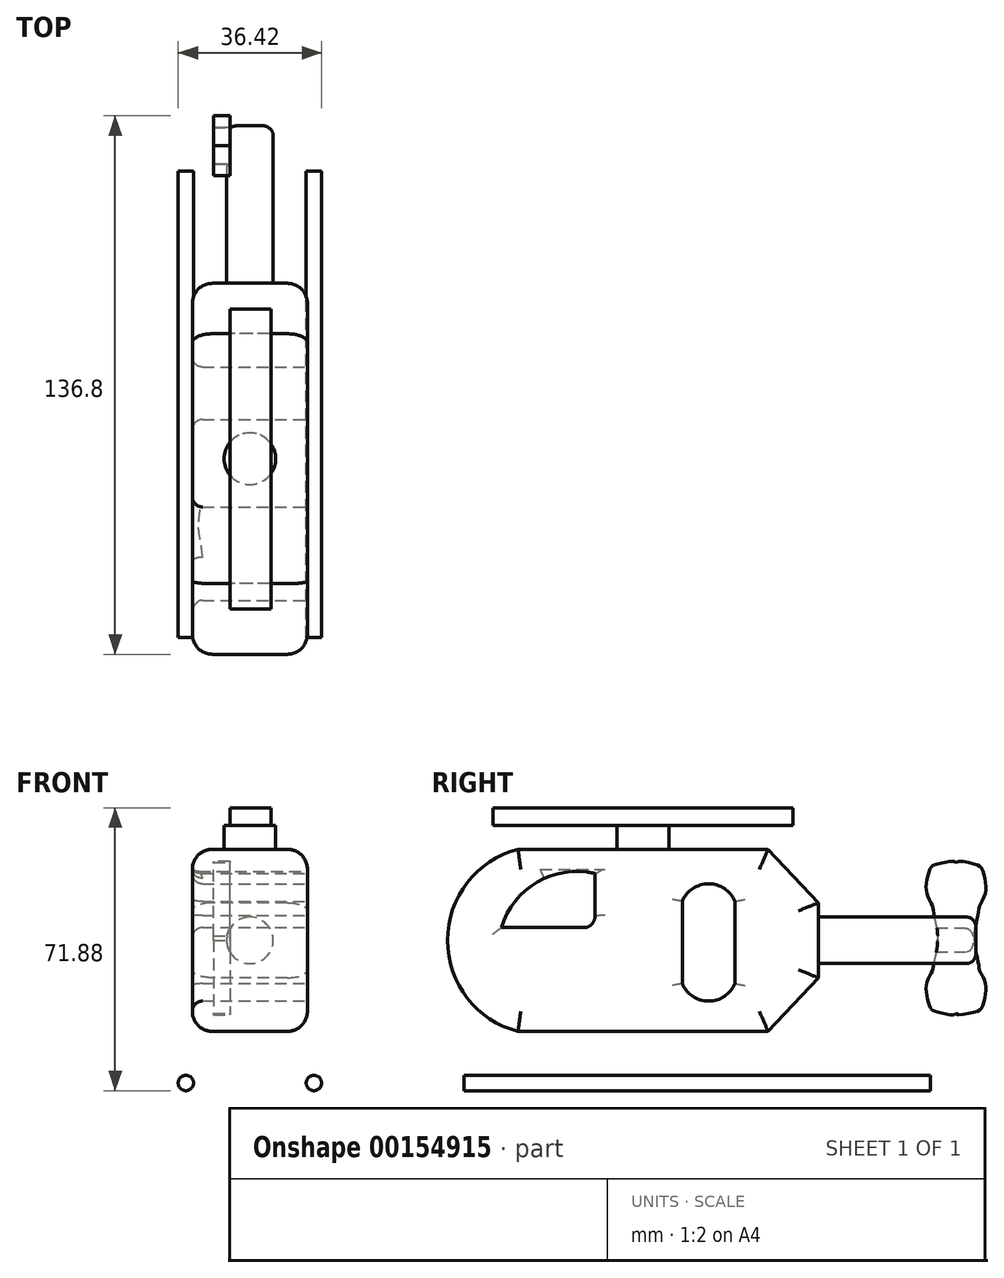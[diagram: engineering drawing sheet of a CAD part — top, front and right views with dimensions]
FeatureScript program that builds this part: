
annotation { "Feature Type Name" : "Feature", "Feature Type Description" : "" }
export const myFeature = defineFeature(function(context is Context, id is Id, definition is map)
    precondition{}
    {
        {
            var Q0;
            Q0=qCreatedBy(makeId("Right.planeOp"),FACE);
            var sketch = newSketch(context, id + "F0", { "sketchPlane" : qUnion([Q0])});
            skLineSegment(sketch, "E0", {"start": v(-45.55, 0) * mm, "end": v(17.95, 0) * mm});
            skLineSegment(sketch, "E1", {"start": v(-45.55, 46.28) * mm, "end": v(17.95, 46.28) * mm});
            skArc(sketch, "E2", {"start": v(-45.55, 46.28) * mm, "mid": v(-63.48, 23.14) * mm, "end": v(-45.55, 0) * mm});
            skLineSegment(sketch, "E3", {"start": v(17.95, 0) * mm, "end": v(30.77, 13.61) * mm});
            skLineSegment(sketch, "E4", {"start": v(-82.92, 23.14) * mm, "end": v(97.5, 23.14) * mm, "construction": true});
            skPoint(sketch, "E4.endSnap0", {"position": v(-63.48, 23.14) * mm});
            skLineSegment(sketch, "E5.MirrorCS", {"start": v(17.95, 46.28) * mm, "end": v(30.77, 32.66) * mm});
            skLineSegment(sketch, "E6", {"start": v(30.77, 32.66) * mm, "end": v(30.77, 13.61) * mm});
            skSolve(sketch);
        }
        {
            var Q0;
            Q0=makeQuery(id+"F0.imprint","IMPRINT",FACE,{"disambiguationData":[TD([[makeQuery(id+"F0.imprint","IMPRINT",EDGE,{"derivedFrom":sQuery(id+"F0.wireOp",EDGE,"E0")}),1.0]])]});
            extrude(context, id + "F1", {"entities" : qUnion([Q0]), "endBound" : BoundingType.SYMMETRIC, "depth" : 29.2 * mm});
        }
        {
            var Q0;
            Q0=makeQuery(id+"F1.opExtrude","CAP_FACE",FACE,{"disambiguationData":[OSD([sQuery(id+"F0.wireOp",EDGE,"E0"),sQuery(id+"F0.wireOp",EDGE,"E1"),sQuery(id+"F0.wireOp",EDGE,"E2"),sQuery(id+"F0.wireOp",EDGE,"E3"),sQuery(id+"F0.wireOp",EDGE,"E5.MirrorCS"),sQuery(id+"F0.wireOp",EDGE,"E6")])],"isStart":false});
            var sketch = newSketch(context, id + "F2", { "sketchPlane" : qUnion([Q0])});
            skLineSegment(sketch, "E7", {"start": v(-49.76, 26.38) * mm, "end": v(-28.82, 26.38) * mm});
            skLineSegment(sketch, "E8", {"start": v(-26.07, 29.47) * mm, "end": v(-26.07, 40.12) * mm});
            skArc(sketch, "E9", {"start": v(-26.07, 40.12) * mm, "mid": v(-40.65, 37.96) * mm, "end": v(-49.76, 26.38) * mm});
            skArc(sketch, "E10", {"start": v(-28.82, 26.38) * mm, "mid": v(-26.75, 27.3) * mm, "end": v(-26.07, 29.47) * mm});
            skLineSegment(sketch, "E11", {"start": v(-3.85, 33.03) * mm, "end": v(-3.85, 12.15) * mm});
            skLineSegment(sketch, "E12", {"start": v(9.5, 33.03) * mm, "end": v(9.5, 12.15) * mm});
            skArc(sketch, "E13", {"start": v(9.5, 33.03) * mm, "mid": v(2.83, 37.49) * mm, "end": v(-3.85, 33.03) * mm});
            skLineSegment(sketch, "E14", {"start": v(-8.12, 22.6) * mm, "end": v(-3.85, 22.6) * mm, "construction": true});
            skPoint(sketch, "E14.startSnap0", {"position": v(-3.85, 22.6) * mm});
            skArc(sketch, "E15.MirrorCS", {"start": v(9.5, 12.15) * mm, "mid": v(2.83, 7.7) * mm, "end": v(-3.85, 12.15) * mm});
            skLineSegment(sketch, "E16.trimOffspring", {"start": v(9.5, 22.6) * mm, "end": v(12.31, 22.6) * mm, "construction": true});
            skSolve(sketch);
        }
        {
            var Q0;
            Q0 = qSketchRegion(id + "F2", true);
            extrude(context, id + "F3", {"entities" : qUnion([Q0]), "operationType" : NewBodyOperationType.ADD, "depth" : 25.4 * mm});
        }
        {
            var Q0;
            Q0=makeQuery(id+"F3.opExtrude","CAP_FACE",FACE,{"disambiguationData":[OSD([sQuery(id+"F2.wireOp",EDGE,"E7"),sQuery(id+"F2.wireOp",EDGE,"E8"),sQuery(id+"F2.wireOp",EDGE,"E9"),sQuery(id+"F2.wireOp",EDGE,"E10")])],"isStart":false});
            extrude(context, id + "F4", {"entities" : qUnion([Q0]), "operationType" : NewBodyOperationType.REMOVE, "oppositeDirection" : true, "depth" : 77.47 * mm});
        }
        {
            var Q0;
            Q0=makeQuery(id+"F3.opExtrude","CAP_FACE",FACE,{"disambiguationData":[OSD([sQuery(id+"F2.wireOp",EDGE,"E11"),sQuery(id+"F2.wireOp",EDGE,"E12"),sQuery(id+"F2.wireOp",EDGE,"E13"),sQuery(id+"F2.wireOp",EDGE,"E15.MirrorCS")])],"isStart":false});
            extrude(context, id + "F5", {"entities" : qUnion([Q0]), "operationType" : NewBodyOperationType.REMOVE, "oppositeDirection" : true, "depth" : 73.02 * mm});
        }
        {
            var Q0;
            Q0=makeQuery(id+"F1.opExtrude","SWEPT_FACE",FACE,{"disambiguationData":[OSD([sQuery(id+"F0.wireOp",EDGE,"E6")])]});
            var sketch = newSketch(context, id + "F6", { "sketchPlane" : qUnion([Q0])});
            skCircle(sketch, "E17", {"center": v(0, 23.14) * mm, "radius": 5.92 * mm});
            skPoint(sketch, "E17.centerSnap0", {"position": v(-14.6, 23.14) * mm});
            skPoint(sketch, "E17.centerSnap1", {"position": v(0, 32.66) * mm});
            skSolve(sketch);
        }
        {
            var Q0;
            Q0=makeQuery(id+"F6.imprint","IMPRINT",FACE,{"disambiguationData":[TD([[makeQuery(id+"F6.imprint","IMPRINT",EDGE,{"derivedFrom":sQuery(id+"F6.wireOp",EDGE,"E17")}),1.0]])]});
            extrude(context, id + "F7", {"entities" : qUnion([Q0]), "operationType" : NewBodyOperationType.ADD, "depth" : 40 * mm});
        }
        {
            var Q0;
            Q0=qCreatedBy(makeId("Right.planeOp"),FACE);
            cPlane(context, id + "F8", {"entities" : qUnion([Q0]), "cplaneType" : CPlaneType.OFFSET, "offset" : 5.08 * mm, "oppositeDirection" : true, "width" : 152.4 * mm, "height" : 152.4 * mm});
        }
        {
            var Q0;
            Q0=qCreatedBy(id+"F8.planeOp",FACE);
            var sketch = newSketch(context, id + "F9", { "sketchPlane" : qUnion([Q0])});
            skCircle(sketch, "E18", {"center": v(65.71, 23.72) * mm, "radius": 4.7 * mm});
            skFitSpline(sketch, "E19", {"points": [v(70.41, 23.72) * mm, v(71.36, 29.92) * mm, v(71.72, 31.94) * mm, v(73.1, 34.83) * mm, v(73.17, 38.08) * mm, v(72.23, 41.47) * mm, v(70.5, 42.48) * mm, v(65.71, 42.91) * mm, v(65.71, 42.35) * mm], "startDerivative": vector(-3.63, 35.2) * mm, "endDerivative": vector(2.3, 5.08) * mm});
            skLineSegment(sketch, "E20", {"start": v(65.71, 42.91) * mm, "end": v(65.71, 6.47) * mm, "construction": true});
            skLineSegment(sketch, "E21", {"start": v(61.01, 23.72) * mm, "end": v(70.41, 23.72) * mm, "construction": true});
            skFitSpline(sketch, "E22.MirrorCS", {"points": [v(61.01, 23.72) * mm, v(60.06, 29.92) * mm, v(59.7, 31.94) * mm, v(58.33, 34.83) * mm, v(58.26, 38.08) * mm, v(59.2, 41.47) * mm, v(60.93, 42.48) * mm, v(65.71, 42.91) * mm, v(65.71, 42.35) * mm], "startDerivative": vector(3.63, 35.2) * mm, "endDerivative": vector(-2.3, 5.08) * mm});
            skFitSpline(sketch, "E23.MirrorCS", {"points": [v(70.41, 23.72) * mm, v(71.36, 17.51) * mm, v(71.72, 15.5) * mm, v(73.1, 12.6) * mm, v(73.17, 9.36) * mm, v(72.23, 5.96) * mm, v(70.5, 4.95) * mm, v(65.71, 4.52) * mm, v(65.71, 5.08) * mm], "startDerivative": vector(-3.63, -35.2) * mm, "endDerivative": vector(2.3, -5.08) * mm});
            skFitSpline(sketch, "E24.MirrorCS", {"points": [v(61.01, 23.72) * mm, v(60.06, 17.51) * mm, v(59.7, 15.5) * mm, v(58.33, 12.6) * mm, v(58.26, 9.36) * mm, v(59.2, 5.96) * mm, v(60.93, 4.95) * mm, v(65.71, 4.52) * mm, v(65.71, 5.08) * mm], "startDerivative": vector(3.63, -35.2) * mm, "endDerivative": vector(-2.3, -5.08) * mm});
            skSolve(sketch);
        }
        {
            var Q0;
            Q0=makeQuery(id+"F1.opExtrude","SWEPT_FACE",FACE,{"disambiguationData":[OSD([sQuery(id+"F0.wireOp",EDGE,"E1")])]});
            var sketch = newSketch(context, id + "F10", { "sketchPlane" : qUnion([Q0])});
            skLineSegment(sketch, "E25", {"start": v(0, 17.95) * mm, "end": v(0, -45.55) * mm, "construction": true});
            skLineSegment(sketch, "E26", {"start": v(14.6, -13.8) * mm, "end": v(-14.6, -13.8) * mm, "construction": true});
            skCircle(sketch, "E27", {"center": v(0, -13.8) * mm, "radius": 6.57 * mm});
            skSolve(sketch);
        }
        {
            var Q0;
            Q0 = qSketchRegion(id + "F10", true);
            extrude(context, id + "F11", {"entities" : qUnion([Q0]), "operationType" : NewBodyOperationType.ADD, "depth" : 6.1 * mm});
        }
        {
            var Q0;
            Q0 = qSketchRegion(id + "F9", true);
            extrude(context, id + "F12", {"entities" : qUnion([Q0]), "operationType" : NewBodyOperationType.ADD, "oppositeDirection" : true, "depth" : 4.2 * mm});
        }
        {
            var Q0;
            Q0=makeQuery(id+"F11.opExtrude","CAP_FACE",FACE,{"disambiguationData":[OSD([sQuery(id+"F10.wireOp",EDGE,"E27")])],"isStart":false});
            var sketch = newSketch(context, id + "F13", { "sketchPlane" : qUnion([Q0])});
            skLineSegment(sketch, "E28.bottom", {"start": v(-5.08, 24.28) * mm, "end": v(5.38, 24.28) * mm});
            skLineSegment(sketch, "E28.top", {"start": v(-5.08, -51.92) * mm, "end": v(5.38, -51.92) * mm});
            skLineSegment(sketch, "E28.left", {"start": v(-5.08, 24.28) * mm, "end": v(-5.08, -51.92) * mm});
            skLineSegment(sketch, "E28.right", {"start": v(5.38, 24.28) * mm, "end": v(5.38, -51.92) * mm});
            skSolve(sketch);
        }
        {
            var Q0;
            {var subQ0=sQuery(id+"F13.wireOp",EDGE,"E28.bottom");Q0=makeQuery(id+"F13.imprint","IMPRINT",FACE,{"disambiguationData":[TD([[makeQuery(id+"F13.imprint","IMPRINT",EDGE,{"derivedFrom":subQ0}),-1.0]])]});}
            var Q1;
            {var subQ0=sQuery(id+"F13.wireOp",EDGE,"E28.left");var subQ1=makeQuery(id+"F11.opExtrude","CAP_EDGE",EDGE,{"disambiguationData":[OSD([sQuery(id+"F10.wireOp",EDGE,"E27")])],"isStart":false});var subQ2=makeQuery(id+"F13.imprint","INTERSECT",VERTEX,{"disambiguationData":[OD(0.0)],"derivedFrom":[subQ1,subQ0]});Q1=makeQuery(id+"F13.imprint","IMPRINT",FACE,{"disambiguationData":[TD([[makeQuery(id+"F13.imprint","IMPRINT",EDGE,{"disambiguationData":[TD([[subQ2,-1.0]])],"derivedFrom":subQ0}),1.0]])]});}
            var Q2;
            {var subQ0=sQuery(id+"F13.wireOp",EDGE,"E28.top");Q2=makeQuery(id+"F13.imprint","IMPRINT",FACE,{"disambiguationData":[TD([[makeQuery(id+"F13.imprint","IMPRINT",EDGE,{"derivedFrom":subQ0}),1.0]])]});}
            extrude(context, id + "F14", {"entities" : qUnion([Q0, Q1, Q2]), "operationType" : NewBodyOperationType.ADD, "depth" : 4.44 * mm});
        }
        {
            var Q0;
            Q0=qCreatedBy(makeId("Front.planeOp"),FACE);
            var sketch = newSketch(context, id + "F15", { "sketchPlane" : qUnion([Q0])});
            skCircle(sketch, "E29", {"center": v(16.26, -13.11) * mm, "radius": 1.95 * mm});
            skCircle(sketch, "E30.MirrorC", {"center": v(-16.26, -13.11) * mm, "radius": 1.95 * mm});
            skSolve(sketch);
        }
        {
            var Q0;
            Q0 = qSketchRegion(id + "F15", true);
            extrude(context, id + "F16", {"entities" : qUnion([Q0]), "endBound" : BoundingType.SYMMETRIC, "depth" : 118.5 * mm});
        }
        {
            var Q0;
            Q0=makeQuery(id+"F1.opExtrude","CAP_EDGE",EDGE,{"disambiguationData":[OSD([sQuery(id+"F0.wireOp",EDGE,"E2")])],"isStart":false});
            var Q1;
            Q1=makeQuery(id+"F1.opExtrude","CAP_EDGE",EDGE,{"disambiguationData":[OSD([sQuery(id+"F0.wireOp",EDGE,"E1")])],"isStart":false});
            var Q2;
            Q2=makeQuery(id+"F1.opExtrude","CAP_EDGE",EDGE,{"disambiguationData":[OSD([sQuery(id+"F0.wireOp",EDGE,"E0")])],"isStart":false});
            var Q3;
            Q3=makeQuery(id+"F1.opExtrude","CAP_EDGE",EDGE,{"disambiguationData":[OSD([sQuery(id+"F0.wireOp",EDGE,"E3")])],"isStart":false});
            var Q4;
            Q4=makeQuery(id+"F1.opExtrude","CAP_EDGE",EDGE,{"disambiguationData":[OSD([sQuery(id+"F0.wireOp",EDGE,"E6")])],"isStart":false});
            var Q5;
            Q5=makeQuery(id+"F1.opExtrude","CAP_EDGE",EDGE,{"disambiguationData":[OSD([sQuery(id+"F0.wireOp",EDGE,"E5.MirrorCS")])],"isStart":false});
            var Q6;
            Q6=makeQuery(id+"F1.opExtrude","CAP_EDGE",EDGE,{"disambiguationData":[OSD([sQuery(id+"F0.wireOp",EDGE,"E6")])],"isStart":true});
            var Q7;
            Q7=makeQuery(id+"F1.opExtrude","CAP_EDGE",EDGE,{"disambiguationData":[OSD([sQuery(id+"F0.wireOp",EDGE,"E5.MirrorCS")])],"isStart":true});
            var Q8;
            Q8=makeQuery(id+"F1.opExtrude","CAP_EDGE",EDGE,{"disambiguationData":[OSD([sQuery(id+"F0.wireOp",EDGE,"E0")])],"isStart":true});
            var Q9;
            Q9=makeQuery(id+"F1.opExtrude","CAP_EDGE",EDGE,{"disambiguationData":[OSD([sQuery(id+"F0.wireOp",EDGE,"E3")])],"isStart":true});
            var Q10;
            Q10=makeQuery(id+"F1.opExtrude","CAP_EDGE",EDGE,{"disambiguationData":[OSD([sQuery(id+"F0.wireOp",EDGE,"E1")])],"isStart":true});
            var Q11;
            Q11=makeQuery(id+"F1.opExtrude","CAP_EDGE",EDGE,{"disambiguationData":[OSD([sQuery(id+"F0.wireOp",EDGE,"E2")])],"isStart":true});
            fillet(context, id + "F17", {"entities" : qUnion([Q0, Q1, Q2, Q3, Q4, Q5, Q6, Q7, Q8, Q9, Q10, Q11]), "radius" : 5.08 * mm, "tangentPropagation" : true, "allowEdgeOverflow" : false});
        }
        {
            var Q0;
            Q0=makeQuery(id+"F5.boolean.opBoolean","INTERSECT",EDGE,{"derivedFrom":[makeQuery(id+"F1.opExtrude","CAP_FACE",FACE,{"disambiguationData":[OSD([sQuery(id+"F0.wireOp",EDGE,"E0"),sQuery(id+"F0.wireOp",EDGE,"E1"),sQuery(id+"F0.wireOp",EDGE,"E2"),sQuery(id+"F0.wireOp",EDGE,"E3"),sQuery(id+"F0.wireOp",EDGE,"E5.MirrorCS"),sQuery(id+"F0.wireOp",EDGE,"E6")])],"isStart":true}),makeQuery(id+"F5.opExtrude","SWEPT_FACE",FACE,{"disambiguationData":[OSD([sQuery(id+"F2.wireOp",EDGE,"E12")])]})]});
            var Q1;
            Q1=makeQuery(id+"F5.boolean.opBoolean","INTERSECT",EDGE,{"derivedFrom":[makeQuery(id+"F1.opExtrude","CAP_FACE",FACE,{"disambiguationData":[OSD([sQuery(id+"F0.wireOp",EDGE,"E0"),sQuery(id+"F0.wireOp",EDGE,"E1"),sQuery(id+"F0.wireOp",EDGE,"E2"),sQuery(id+"F0.wireOp",EDGE,"E3"),sQuery(id+"F0.wireOp",EDGE,"E5.MirrorCS"),sQuery(id+"F0.wireOp",EDGE,"E6")])],"isStart":true}),makeQuery(id+"F5.opExtrude","SWEPT_FACE",FACE,{"disambiguationData":[OSD([sQuery(id+"F2.wireOp",EDGE,"E13")])]})]});
            var Q2;
            Q2=makeQuery(id+"F5.boolean.opBoolean","INTERSECT",EDGE,{"derivedFrom":[makeQuery(id+"F1.opExtrude","CAP_FACE",FACE,{"disambiguationData":[OSD([sQuery(id+"F0.wireOp",EDGE,"E0"),sQuery(id+"F0.wireOp",EDGE,"E1"),sQuery(id+"F0.wireOp",EDGE,"E2"),sQuery(id+"F0.wireOp",EDGE,"E3"),sQuery(id+"F0.wireOp",EDGE,"E5.MirrorCS"),sQuery(id+"F0.wireOp",EDGE,"E6")])],"isStart":true}),makeQuery(id+"F5.opExtrude","SWEPT_FACE",FACE,{"disambiguationData":[OSD([sQuery(id+"F2.wireOp",EDGE,"E11")])]})]});
            var Q3;
            Q3=makeQuery(id+"F5.boolean.opBoolean","INTERSECT",EDGE,{"derivedFrom":[makeQuery(id+"F1.opExtrude","CAP_FACE",FACE,{"disambiguationData":[OSD([sQuery(id+"F0.wireOp",EDGE,"E0"),sQuery(id+"F0.wireOp",EDGE,"E1"),sQuery(id+"F0.wireOp",EDGE,"E2"),sQuery(id+"F0.wireOp",EDGE,"E3"),sQuery(id+"F0.wireOp",EDGE,"E5.MirrorCS"),sQuery(id+"F0.wireOp",EDGE,"E6")])],"isStart":true}),makeQuery(id+"F5.opExtrude","SWEPT_FACE",FACE,{"disambiguationData":[OSD([sQuery(id+"F2.wireOp",EDGE,"E15.MirrorCS")])]})]});
            var Q4;
            Q4=makeQuery(id+"F3.opExtrude","CAP_EDGE",EDGE,{"disambiguationData":[OSD([sQuery(id+"F2.wireOp",EDGE,"E11")])],"isStart":true});
            var Q5;
            Q5=makeQuery(id+"F3.opExtrude","CAP_EDGE",EDGE,{"disambiguationData":[OSD([sQuery(id+"F2.wireOp",EDGE,"E13")])],"isStart":true});
            var Q6;
            Q6=makeQuery(id+"F3.opExtrude","CAP_EDGE",EDGE,{"disambiguationData":[OSD([sQuery(id+"F2.wireOp",EDGE,"E12")])],"isStart":true});
            var Q7;
            Q7=makeQuery(id+"F3.opExtrude","CAP_EDGE",EDGE,{"disambiguationData":[OSD([sQuery(id+"F2.wireOp",EDGE,"E15.MirrorCS")])],"isStart":true});
            fillet(context, id + "F18", {"entities" : qUnion([Q0, Q1, Q2, Q3, Q4, Q5, Q6, Q7]), "radius" : 2.54 * mm, "tangentPropagation" : true, "allowEdgeOverflow" : false});
        }
        {
            var Q0;
            Q0=makeQuery(id+"F3.opExtrude","CAP_EDGE",EDGE,{"disambiguationData":[OSD([sQuery(id+"F2.wireOp",EDGE,"E7")])],"isStart":true});
            var Q1;
            Q1=makeQuery(id+"F3.opExtrude","CAP_EDGE",EDGE,{"disambiguationData":[OSD([sQuery(id+"F2.wireOp",EDGE,"E9")])],"isStart":true});
            var Q2;
            Q2=makeQuery(id+"F3.opExtrude","CAP_EDGE",EDGE,{"disambiguationData":[OSD([sQuery(id+"F2.wireOp",EDGE,"E8")])],"isStart":true});
            var Q3;
            Q3=makeQuery(id+"F3.opExtrude","CAP_EDGE",EDGE,{"disambiguationData":[OSD([sQuery(id+"F2.wireOp",EDGE,"E10")])],"isStart":true});
            var Q4;
            Q4=makeQuery(id+"F4.boolean.opBoolean","INTERSECT",EDGE,{"derivedFrom":[makeQuery(id+"F1.opExtrude","CAP_FACE",FACE,{"disambiguationData":[OSD([sQuery(id+"F0.wireOp",EDGE,"E0"),sQuery(id+"F0.wireOp",EDGE,"E1"),sQuery(id+"F0.wireOp",EDGE,"E2"),sQuery(id+"F0.wireOp",EDGE,"E3"),sQuery(id+"F0.wireOp",EDGE,"E5.MirrorCS"),sQuery(id+"F0.wireOp",EDGE,"E6")])],"isStart":true}),makeQuery(id+"F4.opExtrude","SWEPT_FACE",FACE,{"disambiguationData":[OSD([sQuery(id+"F2.wireOp",EDGE,"E8")])]})]});
            var Q5;
            Q5=makeQuery(id+"F4.boolean.opBoolean","INTERSECT",EDGE,{"derivedFrom":[makeQuery(id+"F1.opExtrude","CAP_FACE",FACE,{"disambiguationData":[OSD([sQuery(id+"F0.wireOp",EDGE,"E0"),sQuery(id+"F0.wireOp",EDGE,"E1"),sQuery(id+"F0.wireOp",EDGE,"E2"),sQuery(id+"F0.wireOp",EDGE,"E3"),sQuery(id+"F0.wireOp",EDGE,"E5.MirrorCS"),sQuery(id+"F0.wireOp",EDGE,"E6")])],"isStart":true}),makeQuery(id+"F4.opExtrude","SWEPT_FACE",FACE,{"disambiguationData":[OSD([sQuery(id+"F2.wireOp",EDGE,"E9")])]})]});
            var Q6;
            Q6=makeQuery(id+"F4.boolean.opBoolean","INTERSECT",EDGE,{"derivedFrom":[makeQuery(id+"F1.opExtrude","CAP_FACE",FACE,{"disambiguationData":[OSD([sQuery(id+"F0.wireOp",EDGE,"E0"),sQuery(id+"F0.wireOp",EDGE,"E1"),sQuery(id+"F0.wireOp",EDGE,"E2"),sQuery(id+"F0.wireOp",EDGE,"E3"),sQuery(id+"F0.wireOp",EDGE,"E5.MirrorCS"),sQuery(id+"F0.wireOp",EDGE,"E6")])],"isStart":true}),makeQuery(id+"F4.opExtrude","SWEPT_FACE",FACE,{"disambiguationData":[OSD([sQuery(id+"F2.wireOp",EDGE,"E7")])]})]});
            var Q7;
            Q7=makeQuery(id+"F4.boolean.opBoolean","INTERSECT",EDGE,{"derivedFrom":[makeQuery(id+"F1.opExtrude","CAP_FACE",FACE,{"disambiguationData":[OSD([sQuery(id+"F0.wireOp",EDGE,"E0"),sQuery(id+"F0.wireOp",EDGE,"E1"),sQuery(id+"F0.wireOp",EDGE,"E2"),sQuery(id+"F0.wireOp",EDGE,"E3"),sQuery(id+"F0.wireOp",EDGE,"E5.MirrorCS"),sQuery(id+"F0.wireOp",EDGE,"E6")])],"isStart":true}),makeQuery(id+"F4.opExtrude","SWEPT_FACE",FACE,{"disambiguationData":[OSD([sQuery(id+"F2.wireOp",EDGE,"E10")])]})]});
            fillet(context, id + "F19", {"entities" : qUnion([Q0, Q1, Q2, Q3, Q4, Q5, Q6, Q7]), "radius" : 2.54 * mm, "tangentPropagation" : true, "allowEdgeOverflow" : false});
        }
        {
            var Q0;
            Q0=makeQuery(id+"F7.opExtrude","CAP_EDGE",EDGE,{"disambiguationData":[OSD([sQuery(id+"F6.wireOp",EDGE,"E17")])],"isStart":false});
            fillet(context, id + "F20", {"entities" : qUnion([Q0]), "radius" : 2.54 * mm, "tangentPropagation" : true, "allowEdgeOverflow" : false});
        }
    });
